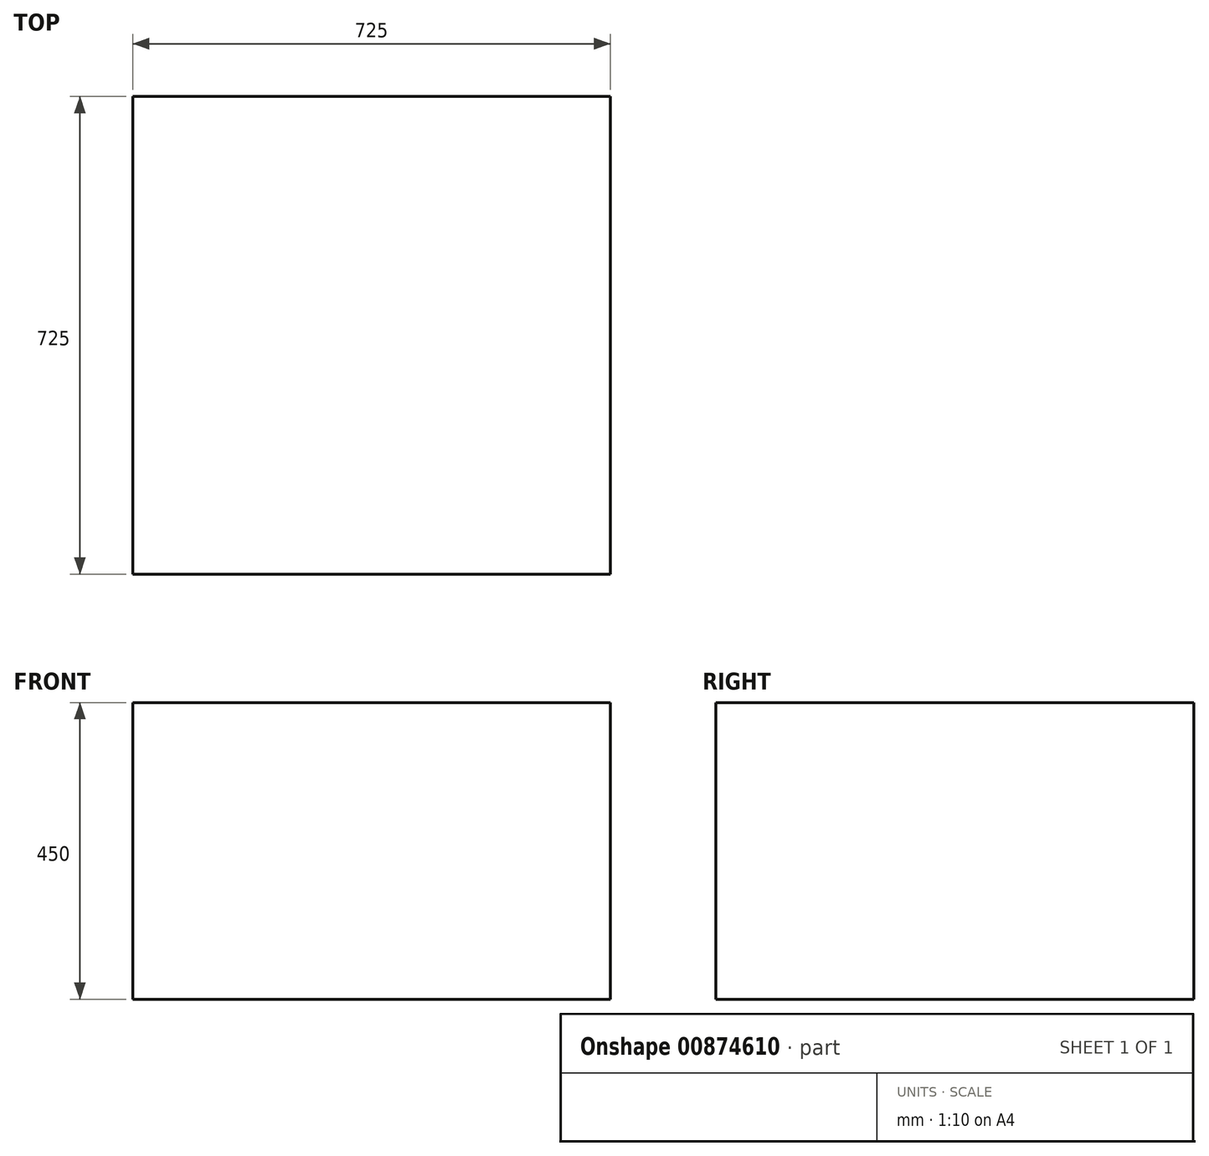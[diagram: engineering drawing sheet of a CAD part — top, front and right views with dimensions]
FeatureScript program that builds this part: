
annotation { "Feature Type Name" : "Feature", "Feature Type Description" : "" }
export const myFeature = defineFeature(function(context is Context, id is Id, definition is map)
    precondition{}
    {
        {
            var Q0;
            Q0=qCreatedBy(makeId("Top.planeOp"),FACE);
            var sketch = newSketch(context, id + "F0", { "sketchPlane" : qUnion([Q0])});
            skLineSegment(sketch, "E0.bottom", {"start": v(0, 0) * mm, "end": v(725, 0) * mm});
            skLineSegment(sketch, "E0.top", {"start": v(0, 725) * mm, "end": v(725, 725) * mm});
            skLineSegment(sketch, "E0.left", {"start": v(0, 0) * mm, "end": v(0, 725) * mm});
            skLineSegment(sketch, "E0.right", {"start": v(725, 0) * mm, "end": v(725, 725) * mm});
            skSolve(sketch);
        }
        {
            var Q0;
            Q0=makeQuery(id+"F0.imprint","IMPRINT",FACE,{"disambiguationData":[TD([[makeQuery(id+"F0.imprint","IMPRINT",EDGE,{"derivedFrom":sQuery(id+"F0.wireOp",EDGE,"E0.bottom")}),1.0]])]});
            extrude(context, id + "F1", {"entities" : qUnion([Q0]), "depth" : 450 * mm, "offsetDistance" : 25 * mm});
        }
    });
